# Revit family: vivaa_pendant_-_vip_7000_vtl_d_00812836_3b8f
name_source: partatom
category: Lighting Fixtures
units: mm (PartAtom-declared; Revit-internal decimal feet)

## family parameters
Cut with Voids When Loaded = No
Host = Face
Light Source = No
Part Type = Normal
Room Calculation Point = No
Round Connector Dimension = Use Diameter
Shared = No

## types (1)
- VIVAA.pendant - VIP 7000/VTL/D (1 x LED, 6700 lm, 2700-6500K)
    Apparent Load = 61 VA
    Approval mark = CE
    CIE Flux Codes = 66 90 97 41 100
    Color Rendering = 90-100
    Color Temperature = 2700-6500K
    Control Gear = Electronic ballast
    Default Elevation = 1800 mm
    Description = VIP 7000/VTL/D|Suspended luminaire|light source:      |luminous flux: 6700 lm|light distribution: Direct/indirect|direct ratio: approx. 40 %|color rendering index (CRI): >= 90|System of protection: IP 20|technology: Two-stage switchable, Continuously dimmable|luminaire body|material: Aluminium|surface: Painted|colour: White|lamp cover: Acrylic (PMMA), Satine|mains lead: 2.00 m Connector 5 pin|Fastening: Ceiling mounted|glare control: Prism aperture|luminance(L65): <= 2800 cd/m|unified glare rating(4H 8H): <=  16|special features: Specified values at approx. 4000 K, Biodynamic light VTL, External control device required for DALI Device Type 6, Separated, direct and indirect light individually adjustable|
    Frequency = 50 Hz, 60 Hz
    Height = 48 mm  [stored 0.15748 ft]
    Lamp = 1 x LED
    Lamp Light Flux = 6700 lm
    Lamp count = 1
    Length = 450 mm
    Luminous efficacy = 110 lm/W
    Manufacturer = Waldmann
    ModVariant = No
    Model = 00812836
    Mounting Place = Ceiling
    Mounting Type = Pendant
    Number of Poles = 1
    OnlyDefault = Yes
    Power Factor = 1
    Product Name = VIVAA.pendant - VIP 7000/VTL/D
    Product group = Suspended luminaire
    ProductGroupID = 9
    Protection Class = Protection class I
    Protection Degree = Degree of protection
    RLX_Detail_Level = 1
    RLX_Emergency_Light_Flux = 0 lm
    RLX_Emergency_Type = 0
    RLX_Emergency_Type_DB = No
    RlxData = <blob elided: 150569 chars, md5=6cd5605d>
    Socket = socket
    Standby Power = 0 W
    System Light Flux = 6700 lm
    System Power = 61 W
    Type Comments = Product without accessories
    Type Image = vivaa_2-0_450_white.jpg
    URL = http://relux.com
    VarID = ---
    Voltage = 230 V
    Voltage Range = 220-240 V
    Weight = 0.00 kg
    Width = 0 mm  [stored 0 ft]

note: [stored X ft] marks values corroborated as IEEE doubles in the binary element streams (Revit-internal decimal feet)

## geometry (parser evidence)
native form markers: Sweep x15
no freeform markers — native parametric forms only
